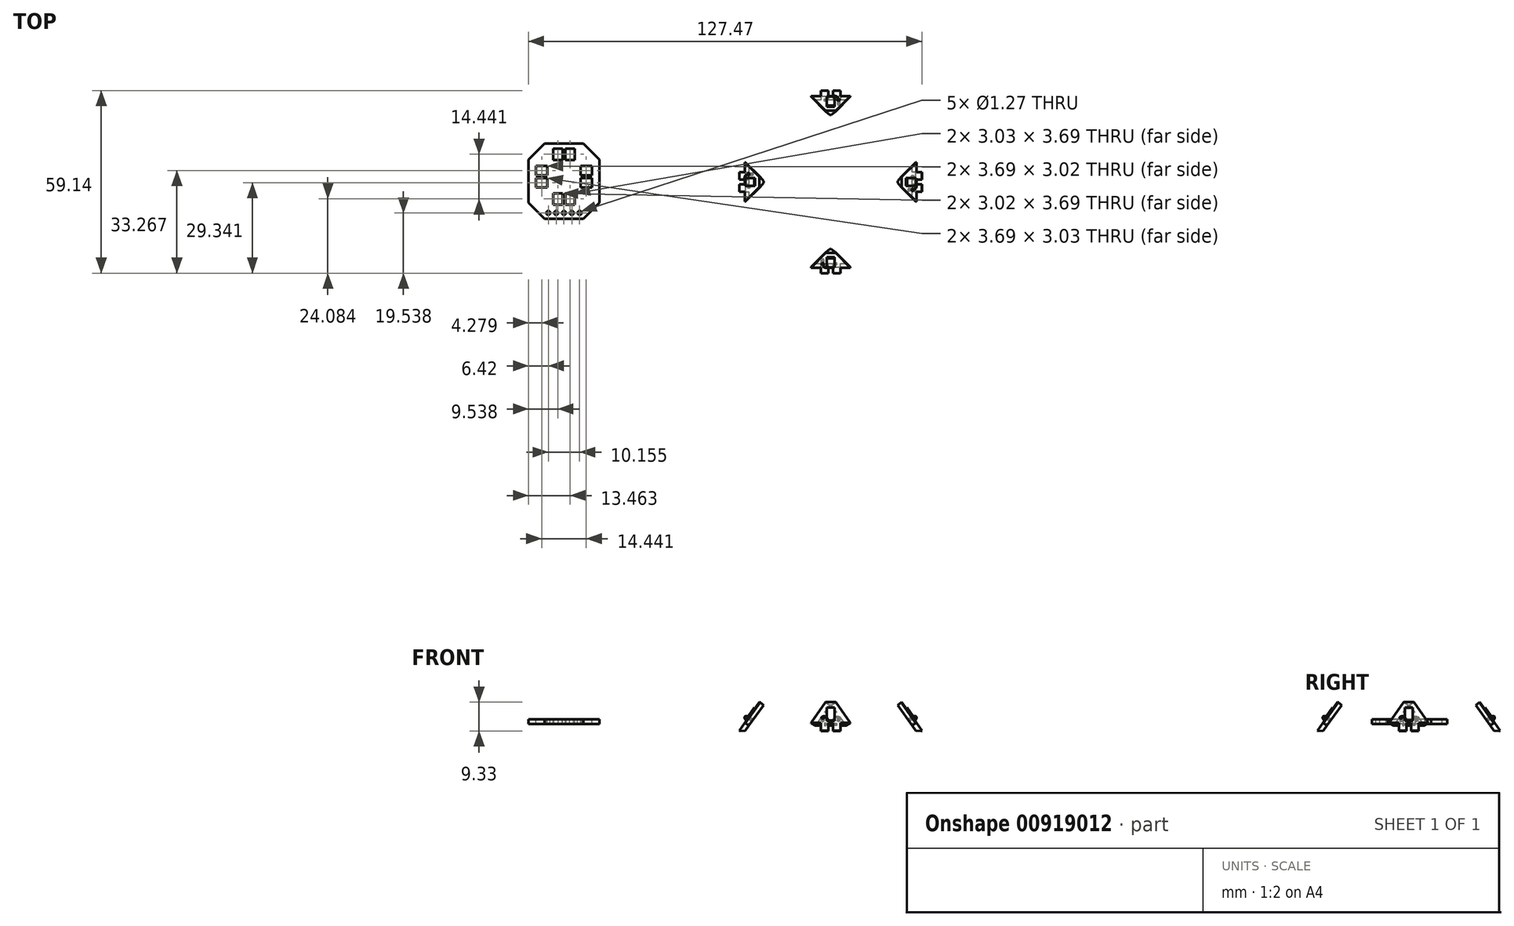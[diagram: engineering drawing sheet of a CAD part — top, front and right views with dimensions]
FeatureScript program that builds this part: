
annotation { "Feature Type Name" : "Feature", "Feature Type Description" : "" }
export const myFeature = defineFeature(function(context is Context, id is Id, definition is map)
    precondition{}
    {
        {
            var Q0;
            Q0=qCreatedBy(makeId("Top.planeOp"),FACE);
            var sketch = newSketch(context, id + "F0", { "sketchPlane" : qUnion([Q0])});
            skLineSegment(sketch, "E0", {"start": v(0, 0) * mm, "end": v(0, 27.35) * mm});
            skLineSegment(sketch, "E1", {"start": v(0, 0) * mm, "end": v(10, 0) * mm});
            skLineSegment(sketch, "E2", {"start": v(10, 0) * mm, "end": v(10, -10) * mm});
            skLineSegment(sketch, "E3", {"start": v(10, -10) * mm, "end": v(0, 0) * mm});
            skLineSegment(sketch, "E4", {"start": v(-61.4, -11.9) * mm, "end": v(-55.11, -11.9) * mm});
            skLineSegment(sketch, "E5", {"start": v(-61.4, -11.9) * mm, "end": v(-67.69, -11.9) * mm});
            skLineSegment(sketch, "E6", {"start": v(-67.68, 12.5) * mm, "end": v(-55.12, 12.5) * mm});
            skLineSegment(sketch, "E7", {"start": v(-49.9, -6.69) * mm, "end": v(-55.11, -11.9) * mm});
            skLineSegment(sketch, "E8", {"start": v(-49.9, 7.28) * mm, "end": v(-55.12, 12.5) * mm});
            skLineSegment(sketch, "E9", {"start": v(-49.9, 7.28) * mm, "end": v(-49.9, -6.69) * mm});
            skLineSegment(sketch, "E10", {"start": v(-72.9, -6.69) * mm, "end": v(-67.69, -11.9) * mm});
            skLineSegment(sketch, "E11", {"start": v(-72.9, 7.28) * mm, "end": v(-67.68, 12.5) * mm});
            skLineSegment(sketch, "E12", {"start": v(-72.9, 7.28) * mm, "end": v(-72.9, -6.69) * mm});
            skLineSegment(sketch, "E13", {"start": v(-61.85, -7.33) * mm, "end": v(-61.85, -3.64) * mm});
            skLineSegment(sketch, "E14", {"start": v(-64.87, -7.33) * mm, "end": v(-64.87, -3.94) * mm});
            skLineSegment(sketch, "E15", {"start": v(-64.87, -3.94) * mm, "end": v(-64.87, -3.64) * mm});
            skLineSegment(sketch, "E16", {"start": v(-64.87, -3.64) * mm, "end": v(-61.85, -3.64) * mm});
            skLineSegment(sketch, "E17", {"start": v(-64.87, -7.33) * mm, "end": v(-61.85, -7.33) * mm});
            skLineSegment(sketch, "E18", {"start": v(-64.87, -7.33) * mm, "end": v(-64.87, -7.03) * mm});
            skLineSegment(sketch, "E19", {"start": v(-60.95, -7.33) * mm, "end": v(-60.95, -3.64) * mm});
            skLineSegment(sketch, "E20", {"start": v(-57.93, -7.33) * mm, "end": v(-57.93, -3.94) * mm});
            skLineSegment(sketch, "E21", {"start": v(-57.93, -3.94) * mm, "end": v(-57.93, -3.64) * mm});
            skLineSegment(sketch, "E22", {"start": v(-57.93, -3.64) * mm, "end": v(-60.95, -3.64) * mm});
            skLineSegment(sketch, "E23", {"start": v(-57.93, -7.33) * mm, "end": v(-60.95, -7.33) * mm});
            skLineSegment(sketch, "E24", {"start": v(-57.93, -7.33) * mm, "end": v(-57.93, -7.03) * mm});
            skLineSegment(sketch, "E25", {"start": v(-52.33, 2.18) * mm, "end": v(-56.03, 2.18) * mm});
            skLineSegment(sketch, "E26", {"start": v(-52.33, 5.2) * mm, "end": v(-55.73, 5.2) * mm});
            skLineSegment(sketch, "E27", {"start": v(-55.73, 5.2) * mm, "end": v(-56.03, 5.2) * mm});
            skLineSegment(sketch, "E28", {"start": v(-56.03, 5.2) * mm, "end": v(-56.03, 2.18) * mm});
            skLineSegment(sketch, "E29", {"start": v(-52.33, 5.2) * mm, "end": v(-52.33, 2.18) * mm});
            skLineSegment(sketch, "E30", {"start": v(-52.33, 5.2) * mm, "end": v(-52.63, 5.2) * mm});
            skLineSegment(sketch, "E31", {"start": v(-52.33, 1.28) * mm, "end": v(-56.03, 1.28) * mm});
            skLineSegment(sketch, "E32", {"start": v(-52.33, -1.74) * mm, "end": v(-55.73, -1.74) * mm});
            skLineSegment(sketch, "E33", {"start": v(-55.73, -1.74) * mm, "end": v(-56.03, -1.74) * mm});
            skLineSegment(sketch, "E34", {"start": v(-56.03, -1.74) * mm, "end": v(-56.03, 1.28) * mm});
            skLineSegment(sketch, "E35", {"start": v(-52.33, -1.74) * mm, "end": v(-52.33, 1.28) * mm});
            skLineSegment(sketch, "E36", {"start": v(-52.33, -1.74) * mm, "end": v(-52.63, -1.74) * mm});
            skLineSegment(sketch, "E37", {"start": v(-61.85, 10.8) * mm, "end": v(-61.85, 7.1) * mm});
            skLineSegment(sketch, "E38", {"start": v(-64.87, 10.8) * mm, "end": v(-64.87, 7.4) * mm});
            skLineSegment(sketch, "E39", {"start": v(-64.87, 7.4) * mm, "end": v(-64.87, 7.1) * mm});
            skLineSegment(sketch, "E40", {"start": v(-64.87, 7.1) * mm, "end": v(-61.85, 7.1) * mm});
            skLineSegment(sketch, "E41", {"start": v(-64.87, 10.8) * mm, "end": v(-61.85, 10.8) * mm});
            skLineSegment(sketch, "E42", {"start": v(-64.87, 10.8) * mm, "end": v(-64.87, 10.5) * mm});
            skLineSegment(sketch, "E43", {"start": v(-60.95, 10.8) * mm, "end": v(-60.95, 7.1) * mm});
            skLineSegment(sketch, "E44", {"start": v(-57.93, 10.8) * mm, "end": v(-57.93, 7.4) * mm});
            skLineSegment(sketch, "E45", {"start": v(-57.93, 7.4) * mm, "end": v(-57.93, 7.1) * mm});
            skLineSegment(sketch, "E46", {"start": v(-57.93, 7.1) * mm, "end": v(-60.95, 7.1) * mm});
            skLineSegment(sketch, "E47", {"start": v(-57.93, 10.8) * mm, "end": v(-60.95, 10.8) * mm});
            skLineSegment(sketch, "E48", {"start": v(-57.93, 10.8) * mm, "end": v(-57.93, 10.5) * mm});
            skLineSegment(sketch, "E49", {"start": v(-70.47, 2.18) * mm, "end": v(-66.77, 2.18) * mm});
            skLineSegment(sketch, "E50", {"start": v(-70.47, 5.2) * mm, "end": v(-67.07, 5.2) * mm});
            skLineSegment(sketch, "E51", {"start": v(-67.07, 5.2) * mm, "end": v(-66.77, 5.2) * mm});
            skLineSegment(sketch, "E52", {"start": v(-66.77, 5.2) * mm, "end": v(-66.77, 2.18) * mm});
            skLineSegment(sketch, "E53", {"start": v(-70.47, 5.2) * mm, "end": v(-70.47, 2.18) * mm});
            skLineSegment(sketch, "E54", {"start": v(-70.47, 5.2) * mm, "end": v(-70.17, 5.2) * mm});
            skLineSegment(sketch, "E55", {"start": v(-70.47, 1.28) * mm, "end": v(-66.77, 1.28) * mm});
            skLineSegment(sketch, "E56", {"start": v(-70.47, -1.74) * mm, "end": v(-67.07, -1.74) * mm});
            skLineSegment(sketch, "E57", {"start": v(-67.07, -1.74) * mm, "end": v(-66.77, -1.74) * mm});
            skLineSegment(sketch, "E58", {"start": v(-66.77, -1.74) * mm, "end": v(-66.77, 1.28) * mm});
            skLineSegment(sketch, "E59", {"start": v(-70.47, -1.74) * mm, "end": v(-70.47, 1.28) * mm});
            skLineSegment(sketch, "E60", {"start": v(-70.47, -1.74) * mm, "end": v(-70.17, -1.74) * mm});
            skCircle(sketch, "E61", {"center": v(-61.4, -10.03) * mm, "radius": 0.64 * mm});
            skCircle(sketch, "E62", {"center": v(-58.86, -10.03) * mm, "radius": 0.64 * mm});
            skCircle(sketch, "E63", {"center": v(-56.32, -10.03) * mm, "radius": 0.64 * mm});
            skCircle(sketch, "E64", {"center": v(-63.94, -10.03) * mm, "radius": 0.64 * mm});
            skCircle(sketch, "E65", {"center": v(-66.48, -10.03) * mm, "radius": 0.64 * mm});
            skSolve(sketch);
        }
        {
            var Q0;
            Q0=sQuery(id+"F0.wireOp",EDGE,"E0");
            cPlane(context, id + "F1", {"entities" : qUnion([Q0]), "cplaneType" : CPlaneType.LINE_ANGLE, "offset" : 25 * mm, "angle" : 54.74 * degree, "oppositeDirection" : true, "width" : 150 * mm, "height" : 150 * mm});
        }
        {
            var Q0;
            Q0=qCreatedBy(id+"F1.planeOp",FACE);
            var sketch = newSketch(context, id + "F2", { "sketchPlane" : qUnion([Q0])});
            skLineSegment(sketch, "E66", {"start": v(6.35, -2.55) * mm, "end": v(1.62, 5.64) * mm});
            skLineSegment(sketch, "E67", {"start": v(-1.62, 5.64) * mm, "end": v(-6.35, -2.55) * mm});
            skLineSegment(sketch, "E68", {"start": v(3.18, -5.64) * mm, "end": v(0.75, -5.64) * mm});
            skLineSegment(sketch, "E69", {"start": v(-0.75, -5.64) * mm, "end": v(-3.18, -5.64) * mm});
            skLineSegment(sketch, "E70", {"start": v(1.62, 5.64) * mm, "end": v(-1.62, 5.64) * mm});
            skLineSegment(sketch, "E71", {"start": v(-3.18, -5.64) * mm, "end": v(-3.18, -2.55) * mm});
            skLineSegment(sketch, "E72", {"start": v(3.18, -5.64) * mm, "end": v(3.18, -2.55) * mm});
            skLineSegment(sketch, "E73", {"start": v(-6.35, -2.55) * mm, "end": v(-3.18, -2.55) * mm});
            skLineSegment(sketch, "E74", {"start": v(3.18, -2.55) * mm, "end": v(6.35, -2.55) * mm});
            skLineSegment(sketch, "E75", {"start": v(-0.75, -5.64) * mm, "end": v(-0.75, -2.55) * mm});
            skCircle(sketch, "E76", {"center": v(-2.55, -0.48) * mm, "radius": 0.42 * mm});
            skLineSegment(sketch, "E77", {"start": v(-0.75, -2.55) * mm, "end": v(0.75, -2.55) * mm});
            skLineSegment(sketch, "E78", {"start": v(0.75, -2.55) * mm, "end": v(0.75, -5.64) * mm});
            skLineSegment(sketch, "E79", {"start": v(1.96, -2.55) * mm, "end": v(1.46, -2.55) * mm});
            skLineSegment(sketch, "E80", {"start": v(1.46, -2.55) * mm, "end": v(1.46, -2.05) * mm});
            skLineSegment(sketch, "E81", {"start": v(1.46, -2.05) * mm, "end": v(1.96, -2.05) * mm});
            skLineSegment(sketch, "E82", {"start": v(1.96, -2.05) * mm, "end": v(1.96, -2.55) * mm});
            skSolve(sketch);
        }
        {
            var Q0;
            Q0=qSketchRegion(id+"F2",true);
            var Q1;
            Q1=makeQuery(id+"F2.imprint","IMPRINT",FACE,{"disambiguationData":[TD([[makeQuery(id+"F2.imprint","IMPRINT",EDGE,{"derivedFrom":sQuery(id+"F2.wireOp",EDGE,"E79")}),-1.0]])]});
            extrude(context, id + "F3", {"entities" : qUnion([Q0, Q1]), "depth" : 1.6 * mm, "offsetDistance" : 25 * mm});
        }
        {
            var Q0;
            Q0=makeQuery(id+"F2.imprint","IMPRINT",FACE,{"disambiguationData":[TD([[makeQuery(id+"F2.imprint","IMPRINT",EDGE,{"derivedFrom":sQuery(id+"F2.wireOp",EDGE,"E79")}),-1.0]])]});
            extrude(context, id + "F4", {"entities" : qUnion([Q0]), "operationType" : NewBodyOperationType.REMOVE, "depth" : .6 * mm, "offsetDistance" : 25 * mm});
        }
        {
            var Q0;
            Q0=qCreatedBy(makeId("Right.planeOp"),FACE);
            cPlane(context, id + "F5", {"entities" : qUnion([Q0]), "cplaneType" : CPlaneType.OFFSET, "offset" : 25 * mm, "width" : 150 * mm, "height" : 150 * mm});
        }
        {
            var Q0;
            Q0=qCreatedBy(id+"F5.planeOp",FACE);
            var sketch = newSketch(context, id + "F6", { "sketchPlane" : qUnion([Q0])});
            skLineSegment(sketch, "E83", {"start": v(0, 0) * mm, "end": v(0, 26.14) * mm});
            skSolve(sketch);
        }
        {
            var Q0;
            Q0=qCreatedBy(makeId("Front.planeOp"),FACE);
            var sketch = newSketch(context, id + "F7", { "sketchPlane" : qUnion([Q0])});
            skPoint(sketch, "E84.0", {"position": v(-4.57, -3.69) * mm});
            skPoint(sketch, "E84.1", {"position": v(-3.26, -4.6) * mm});
            skPoint(sketch, "E84.2", {"position": v(-2.37, -3.35) * mm});
            skLineSegment(sketch, "E85", {"start": v(-3.26, -4.6) * mm, "end": v(-4.57, -3.69) * mm});
            skLineSegment(sketch, "E86", {"start": v(-4.57, -3.69) * mm, "end": v(-4.4, -3.8) * mm});
            skLineSegment(sketch, "E87", {"start": v(-3.26, -4.6) * mm, "end": v(-2.62, -3.71) * mm});
            skLineSegment(sketch, "E88", {"start": v(-2.62, -3.71) * mm, "end": v(-4.4, -3.8) * mm});
            skSolve(sketch);
        }
        {
            var Q0;
            Q0=makeQuery(id+"F7.imprint","IMPRINT",FACE,{"disambiguationData":[TD([[makeQuery(id+"F7.imprint","IMPRINT",EDGE,{"derivedFrom":sQuery(id+"F7.wireOp",EDGE,"E85")}),-1.0]])]});
            extrude(context, id + "F8", {"entities" : qUnion([Q0]), "operationType" : NewBodyOperationType.REMOVE, "endBound" : BoundingType.SYMMETRIC, "oppositeDirection" : true, "depth" : 25 * mm, "offsetDistance" : 25 * mm});
        }
        {
            var Q0;
            Q0=makeQuery(id+"F3.opExtrude","SWEPT_FACE",FACE,{"disambiguationData":[OSD([sQuery(id+"F2.wireOp",EDGE,"E70")])]});
            var sketch = newSketch(context, id + "F9", { "sketchPlane" : qUnion([Q0])});
            skPoint(sketch, "E89.0", {"position": v(0, -1.62) * mm});
            skPoint(sketch, "E89.1", {"position": v(-1.6, -1.62) * mm});
            skPoint(sketch, "E89.2", {"position": v(0, 1.62) * mm});
            skPoint(sketch, "E89.3", {"position": v(-1.6, 1.62) * mm});
            skLineSegment(sketch, "E90", {"start": v(0, -1.62) * mm, "end": v(0, -0.22) * mm});
            skLineSegment(sketch, "E91", {"start": v(0, -1.62) * mm, "end": v(-1.4, -1.62) * mm});
            skLineSegment(sketch, "E92", {"start": v(0, 1.62) * mm, "end": v(0, 0.22) * mm});
            skLineSegment(sketch, "E93", {"start": v(0, 1.62) * mm, "end": v(-1.4, 1.62) * mm});
            skLineSegment(sketch, "E94", {"start": v(-1.4, 1.62) * mm, "end": v(0, 0.22) * mm});
            skLineSegment(sketch, "E95", {"start": v(0, -0.22) * mm, "end": v(-1.4, -1.62) * mm});
            skSolve(sketch);
        }
        {
            var Q0;
            Q0=makeQuery(id+"F9.imprint","IMPRINT",FACE,{"disambiguationData":[TD([[makeQuery(id+"F9.imprint","IMPRINT",EDGE,{"derivedFrom":sQuery(id+"F9.wireOp",EDGE,"E92")}),1.0]])]});
            var Q1;
            Q1=sQuery(id+"F2.wireOp",EDGE,"E67");
            sweep(context, id + "F10", {"operationType" : NewBodyOperationType.REMOVE, "profiles" : qUnion([Q0]), "path" : qUnion([Q1])});
        }
        {
            var Q0;
            Q0=makeQuery(id+"F9.imprint","IMPRINT",FACE,{"disambiguationData":[TD([[makeQuery(id+"F9.imprint","IMPRINT",EDGE,{"derivedFrom":sQuery(id+"F9.wireOp",EDGE,"E90")}),1.0]])]});
            var Q1;
            Q1=sQuery(id+"F2.wireOp",EDGE,"E66");
            sweep(context, id + "F11", {"operationType" : NewBodyOperationType.REMOVE, "profiles" : qUnion([Q0]), "path" : qUnion([Q1])});
        }
        {
            var Q0;
            Q0=makeQuery(id+"F3.opExtrude","CAP_FACE",FACE,{"disambiguationData":[OSD([sQuery(id+"F2.wireOp",EDGE,"E66"),sQuery(id+"F2.wireOp",EDGE,"E67"),sQuery(id+"F2.wireOp",EDGE,"E68"),sQuery(id+"F2.wireOp",EDGE,"E69"),sQuery(id+"F2.wireOp",EDGE,"E70"),sQuery(id+"F2.wireOp",EDGE,"E71"),sQuery(id+"F2.wireOp",EDGE,"E72"),sQuery(id+"F2.wireOp",EDGE,"E73"),sQuery(id+"F2.wireOp",EDGE,"E74"),sQuery(id+"F2.wireOp",EDGE,"E75"),sQuery(id+"F2.wireOp",EDGE,"E76"),sQuery(id+"F2.wireOp",EDGE,"E77"),sQuery(id+"F2.wireOp",EDGE,"E78")])],"isStart":false});
            var sketch = newSketch(context, id + "F12", { "sketchPlane" : qUnion([Q0])});
            skPoint(sketch, "E96.0", {"position": v(0, -2.55) * mm});
            skLineSegment(sketch, "E97", {"start": v(0, -2.55) * mm, "end": v(0, -2.55) * mm});
            skLineSegment(sketch, "E98", {"start": v(0, -2.55) * mm, "end": v(0, -1.86) * mm});
            skLineSegment(sketch, "E99", {"start": v(0, -1.86) * mm, "end": v(1.25, -1.86) * mm});
            skLineSegment(sketch, "E100", {"start": v(1.25, -1.86) * mm, "end": v(1.25, 3.24) * mm});
            skLineSegment(sketch, "E101", {"start": v(1.25, 3.24) * mm, "end": v(-1.25, 3.24) * mm});
            skLineSegment(sketch, "E102", {"start": v(-1.25, 3.24) * mm, "end": v(-1.25, -1.86) * mm});
            skLineSegment(sketch, "E103", {"start": v(-1.25, -1.86) * mm, "end": v(0, -1.86) * mm});
            skCircle(sketch, "E104", {"center": v(-0.98, -1.54) * mm, "radius": 0.12 * mm});
            skCircle(sketch, "E105.0", {"center": v(-2.55, -0.48) * mm, "radius": 0.42 * mm, "construction": true});
            skLineSegment(sketch, "E106", {"start": v(-2.55, -0.48) * mm, "end": v(-0.98, -1.54) * mm, "construction": true});
            skSolve(sketch);
        }
        {
            var Q0;
            Q0=makeQuery(id+"F12.imprint","IMPRINT",FACE,{"disambiguationData":[TD([[makeQuery(id+"F12.imprint","IMPRINT",EDGE,{"derivedFrom":sQuery(id+"F12.wireOp",EDGE,"E99")}),1.0]])]});
            var Q1;
            Q1=makeQuery(id+"F12.imprint","IMPRINT",FACE,{"disambiguationData":[TD([[makeQuery(id+"F12.imprint","IMPRINT",EDGE,{"derivedFrom":sQuery(id+"F12.wireOp",EDGE,"E104")}),1.0]])]});
            extrude(context, id + "F13", {"entities" : qUnion([Q0, Q1]), "operationType" : NewBodyOperationType.ADD, "depth" : 0.4 * mm, "offsetDistance" : 25 * mm});
        }
        {
            var Q0;
            Q0=sQuery(id+"F12.wireOp",EDGE,"E106");
            cPlane(context, id + "F14", {"entities" : qUnion([Q0]), "cplaneType" : CPlaneType.LINE_ANGLE, "offset" : 25 * mm, "angle" : 35.26 * degree, "oppositeDirection" : true, "width" : 150 * mm, "height" : 150 * mm});
        }
        {
            var Q0;
            Q0=qCreatedBy(id+"F14.planeOp",FACE);
            var sketch = newSketch(context, id + "F15", { "sketchPlane" : qUnion([Q0])});
            skPoint(sketch, "E107.0", {"position": v(-0.62, -2.26) * mm});
            skPoint(sketch, "E107.1", {"position": v(-1.35, -0.51) * mm});
            skEllipse(sketch, "E108.0", {"center": v(-0.62, -2.26) * mm, "majorRadius": 0.42 * mm, "minorRadius": 0.04 * mm, "majorAxis": v(-0.38, 0.92), "construction": true});
            skFitSpline(sketch, "E109", {"points": [v(-1.35, -0.51) * mm, v(-1.83, -0.83) * mm, v(-2.01, -1.48) * mm, v(-1.75, -2.12) * mm, v(-1.33, -2.35) * mm, v(-0.62, -2.26) * mm, v(0.39, -1.85) * mm], "startDerivative": vector(-3.6, -1.57) * mm, "endDerivative": vector(4.68, 2.02) * mm});
            skSolve(sketch);
        }
        {
            var Q0;
            Q0=makeQuery(id+"F12.imprint","IMPRINT",FACE,{"disambiguationData":[TD([[makeQuery(id+"F12.imprint","IMPRINT",EDGE,{"derivedFrom":sQuery(id+"F12.wireOp",EDGE,"E104")}),1.0]])]});
            var Q1;
            Q1=sQuery(id+"F15.wireOp",EDGE,"E109");
            sweep(context, id + "F16", {"operationType" : NewBodyOperationType.ADD, "profiles" : qUnion([Q0]), "path" : qUnion([Q1])});
        }
        {
            var Q0;
            Q0=makeQuery(id+"F3.opExtrude","SWEPT_BODY",BODY,{"disambiguationData":[OSD([sQuery(id+"F2.wireOp",EDGE,"E66"),sQuery(id+"F2.wireOp",EDGE,"E67"),sQuery(id+"F2.wireOp",EDGE,"E68"),sQuery(id+"F2.wireOp",EDGE,"E69"),sQuery(id+"F2.wireOp",EDGE,"E70"),sQuery(id+"F2.wireOp",EDGE,"E71"),sQuery(id+"F2.wireOp",EDGE,"E72"),sQuery(id+"F2.wireOp",EDGE,"E73"),sQuery(id+"F2.wireOp",EDGE,"E74"),sQuery(id+"F2.wireOp",EDGE,"E75"),sQuery(id+"F2.wireOp",EDGE,"E76"),sQuery(id+"F2.wireOp",EDGE,"E77"),sQuery(id+"F2.wireOp",EDGE,"E78")])]});
            var Q1;
            Q1=sQuery(id+"F6.wireOp",EDGE,"E83");
            circularPattern(context, id + "F17", {"entities" : qUnion([Q0]), "axis" : qUnion([Q1]), "angle" : 360 * degree, "instanceCount" : 4, "equalSpace" : true});
        }
        {
            var Q0;
            Q0=makeQuery(id+"F0.imprint","IMPRINT",FACE,{"disambiguationData":[TD([[makeQuery(id+"F0.imprint","IMPRINT",EDGE,{"derivedFrom":sQuery(id+"F0.wireOp",EDGE,"E4")}),1.0]])]});
            extrude(context, id + "F18", {"entities" : qUnion([Q0]), "oppositeDirection" : true, "depth" : 1.6 * mm, "offsetDistance" : 25 * mm});
        }
    });
